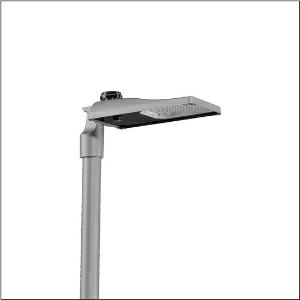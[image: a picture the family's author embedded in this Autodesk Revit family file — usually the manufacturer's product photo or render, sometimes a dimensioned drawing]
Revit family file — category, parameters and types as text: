
# Revit family: streetlight_sl_31_mini___st1_0a_5xh2d3bm08ha_2d93
name_source: partatom
category: Lighting Fixtures
units: mm (PartAtom-declared; Revit-internal decimal feet)

## family parameters
Cut with Voids When Loaded = No
Host = Face
Light Source = No
Part Type = Normal
Room Calculation Point = No
Round Connector Dimension = Use Diameter
Shared = No

## types (1)
- --- (1 x LED, 9230 lm, 68.2 W, 3000K)
    Apparent Load = 68 VA
    CIE Flux Codes = 37 72 97 100 100
    Color Rendering = 70
    Color Temperature = 3000K
    Default Elevation = 1800 mm
    Description = Streetlight SL 31 mini, mast luminaire, primary light control with lens, of PMMA, primary optical cover: cover, of toughened safety glass, transparent, light distribution: ST1.0a, light emission: direct distribution, primary light characteristic: asymmetric, installation type: post-top, side-entry, LED, High Power LED, rated luminous flux: 9.230lm, luminous efficacy: 135lm/W, light colour: 730, colour temperature: 3000K, control: presetting dimming linear, flexible luminous flux parameterisation, time-dependent luminous flux control, constant luminous flux control, intelligent temperature release in ECG and LED module, overheat protection, with cable H07RN-F 3x 1.5mm², mains connection: 220..240V, AC, 50/60Hz, connection cable pre-assembled, cable length: 8,5m, start of lifetime: 68W, end of service life: 74W, reduction: 30W, luminaire housing, of diecast aluminium, powder-coated, Siteco® metallic grey (DB 702S), corrosivity category C5 high according to DIN EN ISO 12944, no sealing on luminaire upper side, inclination: -15°..+20° (post-top) | -20°..+20° (side-entry), adjustable in 5° steps, mast flange (76/60mm) included as standard, multi-level sealing system, sealing non-destructively replaceable, Smart Interface below, protection rating (complete): IP66, insulation class (complete): insulation class I (protective earthing), certification: CE, ENEC, ENEC+, VDE, UKCA, impact resistance: IK09, permissible operating ambient temperature for outdoor applications: -40..+50°C, standard-compliant lighting for roads and squares, packaging unit: 1 piece

Light Distribution: ST1.0a
    Height = 76 mm
    Lamp = 1 x LED
    Lamp Light Flux = 9230 lm
    Lamp Power = 68.2 W
    Lamp count = 1
    Length = 547 mm
    Luminous efficacy = 135 lm/W
    Manufacturer = Siteco
    ModVariant = No
    Model = 5XH2D3BM08HA
    Number of Poles = 1
    OnlyDefault = Yes
    Power Factor = 1
    Product Name = Streetlight SL 31 mini | ST1.0a
    Product group = mast luminaire | pylon top
    ProductGroupID = 6100
    Protection Class = Protection class I
    Protection Degree = IP 66
    RLX_Detail_Level = 1
    RLX_Emergency_Light_Flux = 0 lm
    RLX_Emergency_Type = 0
    RLX_Emergency_Type_DB = No
    RlxData = <blob elided: 40273 chars, md5=e212b12b>
    Socket = socket
    Standby Power = 0 W
    System Light Flux = 9230 lm
    System Power = 68 W
    Type Comments = factory setting: luminous flux: 100 % | dim-lin: 254 | 692 mA
    Type Image = l_1300324.jpg
    URL = http://relux.com
    VarID = @adj_012417
    Voltage = 0 V
    Weight = 0.00 kg
    Width = 265 mm

## geometry (parser evidence)
native form markers: Blend x4, Sweep x11
no freeform markers — native parametric forms only
